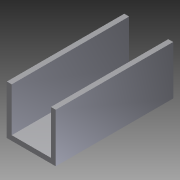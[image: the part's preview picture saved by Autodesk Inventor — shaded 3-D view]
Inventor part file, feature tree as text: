
AUTODESK INVENTOR PART (.ipt)
format: ipt  version: 2012 (Build 160160000, 160)  size: 79,360 bytes
history: native  units: in
note: dims shown in document units (in); Inventor stores cm internally (conversion verified against a paired STEP export)
features: extrude x1, sketch x1
ambient origin geometry x8: Origin, YZ Plane, XZ Plane, XY Plane, X Axis, Y Axis, Z Axis, Center Point
bodies: Solid1 (feature_tree)
feature tree (2):
  extrude  "Extrusion1"  Depth=0.125in
  sketch  "Sketch1"  dims[d0=0.125in d2=0.125in d3=0.125in d4=1.25in d5=1.25in d6=3.0in d7=0.0in]
